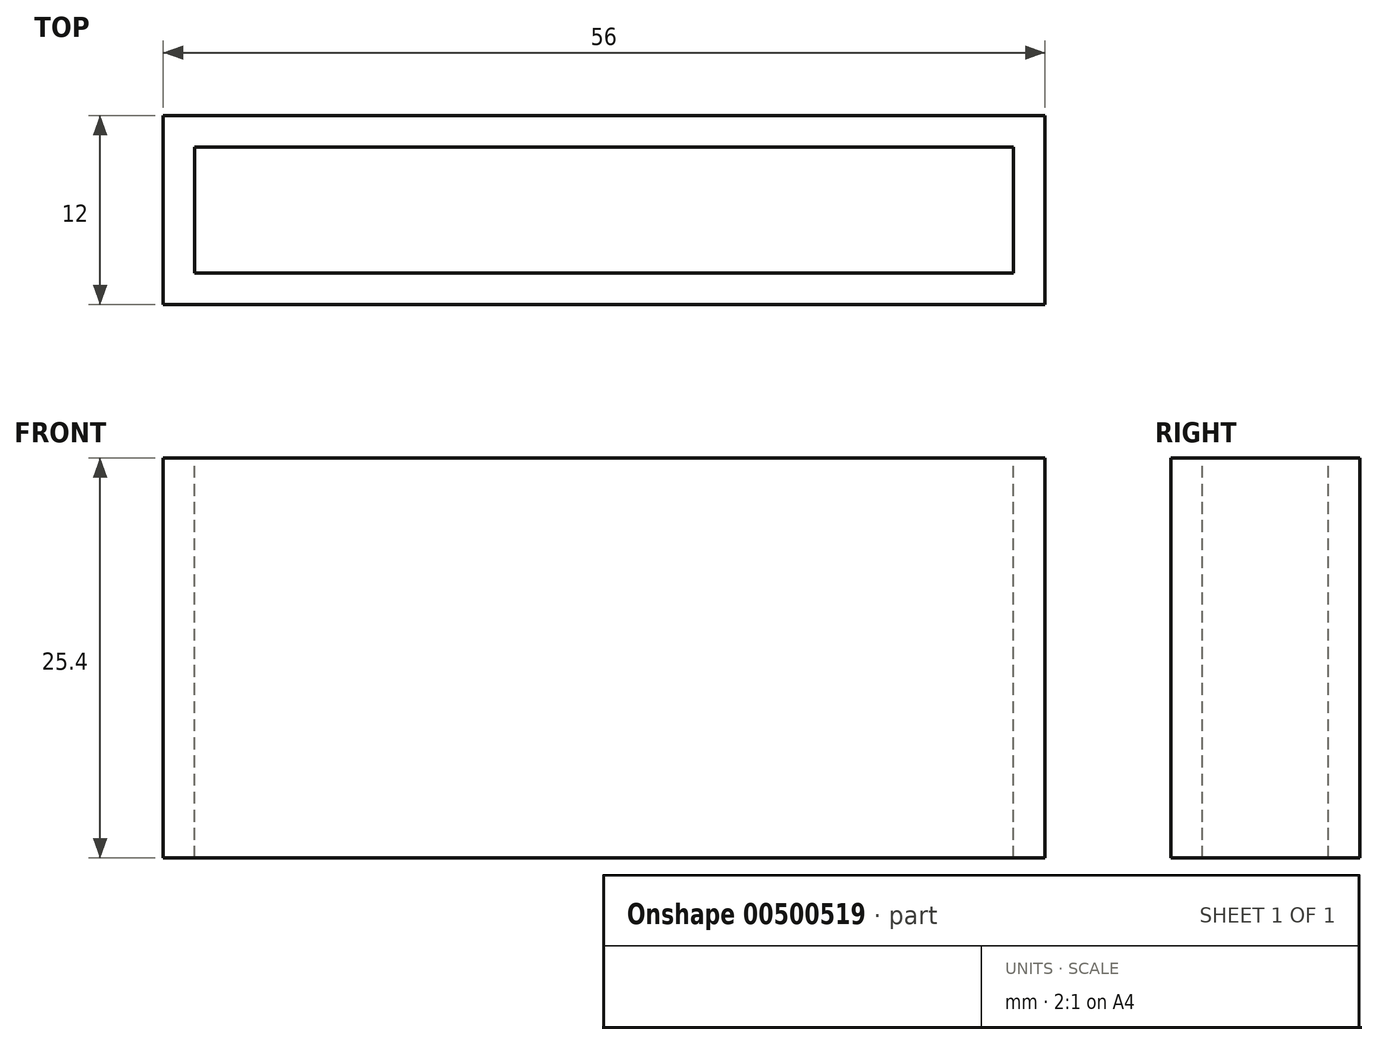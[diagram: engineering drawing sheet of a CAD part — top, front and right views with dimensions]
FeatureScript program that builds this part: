
annotation { "Feature Type Name" : "Feature", "Feature Type Description" : "" }
export const myFeature = defineFeature(function(context is Context, id is Id, definition is map)
    precondition{}
    {
        {
            var Q0;
            Q0=qCreatedBy(makeId("Top.planeOp"),FACE);
            var sketch = newSketch(context, id + "F0", { "sketchPlane" : qUnion([Q0])});
            skLineSegment(sketch, "E0.bottom", {"start": v(-11.2, -11.74) * mm, "end": v(40.8, -11.74) * mm});
            skLineSegment(sketch, "E0.top", {"start": v(-11.2, -19.74) * mm, "end": v(40.8, -19.74) * mm});
            skLineSegment(sketch, "E0.left", {"start": v(-11.2, -11.74) * mm, "end": v(-11.2, -19.74) * mm});
            skLineSegment(sketch, "E0.right", {"start": v(40.8, -11.74) * mm, "end": v(40.8, -19.74) * mm});
            skLineSegment(sketch, "E1.0", {"start": v(-13.2, -9.74) * mm, "end": v(-13.2, -21.74) * mm});
            skLineSegment(sketch, "E1.1", {"start": v(-13.2, -9.74) * mm, "end": v(42.8, -9.74) * mm});
            skLineSegment(sketch, "E1.2", {"start": v(42.8, -9.74) * mm, "end": v(42.8, -21.74) * mm});
            skLineSegment(sketch, "E1.3", {"start": v(-13.2, -21.74) * mm, "end": v(42.8, -21.74) * mm});
            skSolve(sketch);
        }
        {
            var Q0;
            Q0=sQuery(id+"F0.wireOp",EDGE,"E1.1");
            var Q1;
            Q1=sQuery(id+"F0.wireOp",EDGE,"E1.2");
            var Q2;
            Q2=sQuery(id+"F0.wireOp",EDGE,"E1.3");
            var Q3;
            Q3=sQuery(id+"F0.wireOp",EDGE,"E1.0");
            var Q4;
            Q4=sQuery(id+"F0.wireOp",EDGE,"E0.left");
            var Q5;
            Q5=sQuery(id+"F0.wireOp",EDGE,"E0.bottom");
            var Q6;
            Q6=sQuery(id+"F0.wireOp",EDGE,"E0.top");
            var Q7;
            Q7=sQuery(id+"F0.wireOp",EDGE,"E0.right");
            extrude(context, id + "F1", {"bodyType" : ToolBodyType.SURFACE, "surfaceEntities" : qUnion([Q0, Q1, Q2, Q3, Q4, Q5, Q6, Q7]), "depth" : 25.4 * mm});
        }
    });
